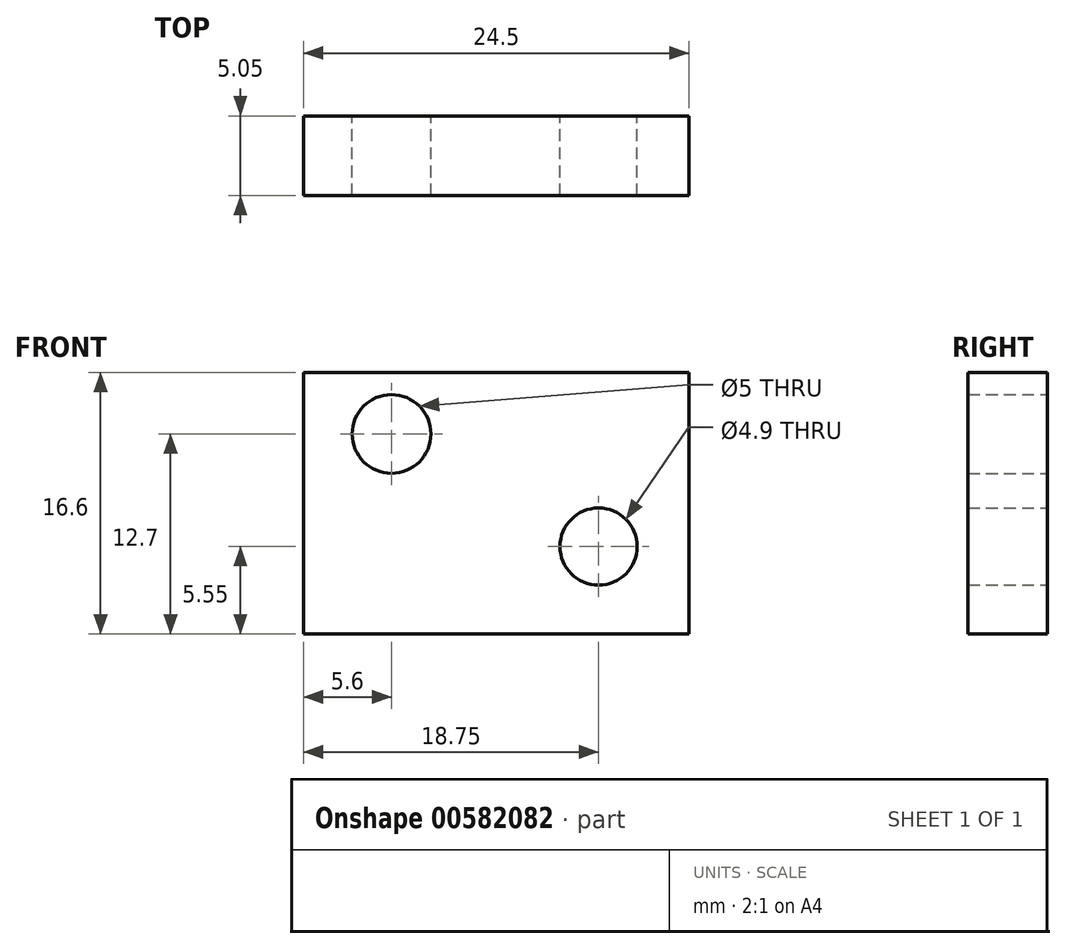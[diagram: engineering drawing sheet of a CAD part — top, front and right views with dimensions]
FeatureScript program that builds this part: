
annotation { "Feature Type Name" : "Feature", "Feature Type Description" : "" }
export const myFeature = defineFeature(function(context is Context, id is Id, definition is map)
    precondition{}
    {
        {
            var Q0;
            Q0=qCreatedBy(makeId("Front.planeOp"),FACE);
            var sketch = newSketch(context, id + "F0", { "sketchPlane" : qUnion([Q0])});
            skLineSegment(sketch, "E0.bottom", {"start": v(-12.25, 8.3) * mm, "end": v(12.25, 8.3) * mm});
            skLineSegment(sketch, "E0.top", {"start": v(-12.25, -8.3) * mm, "end": v(12.25, -8.3) * mm});
            skLineSegment(sketch, "E0.left", {"start": v(-12.25, 8.3) * mm, "end": v(-12.25, -8.3) * mm});
            skLineSegment(sketch, "E0.right", {"start": v(12.25, 8.3) * mm, "end": v(12.25, -8.3) * mm});
            skPoint(sketch, "E0.middle", {"position": v(0, 0) * mm});
            skCircle(sketch, "E1", {"center": v(-6.65, 4.4) * mm, "radius": 2.5 * mm});
            skCircle(sketch, "E2", {"center": v(6.5, -2.75) * mm, "radius": 2.45 * mm});
            skPoint(sketch, "E3", {"position": v(8.95, -2.75) * mm});
            skPoint(sketch, "E4", {"position": v(6.5, -5.2) * mm});
            skPoint(sketch, "E5", {"position": v(-6.65, 6.9) * mm});
            skPoint(sketch, "E6", {"position": v(-9.15, 4.4) * mm});
            skSolve(sketch);
        }
        {
            var Q0;
            Q0=makeQuery(id+"F0.imprint","IMPRINT",FACE,{"disambiguationData":[TD([[makeQuery(id+"F0.imprint","IMPRINT",EDGE,{"derivedFrom":sQuery(id+"F0.wireOp",EDGE,"E0.bottom")}),-1.0]])]});
            extrude(context, id + "F1", {"entities" : qUnion([Q0]), "depth" : 5.05 * mm, "offsetDistance" : 25 * mm});
        }
    });
